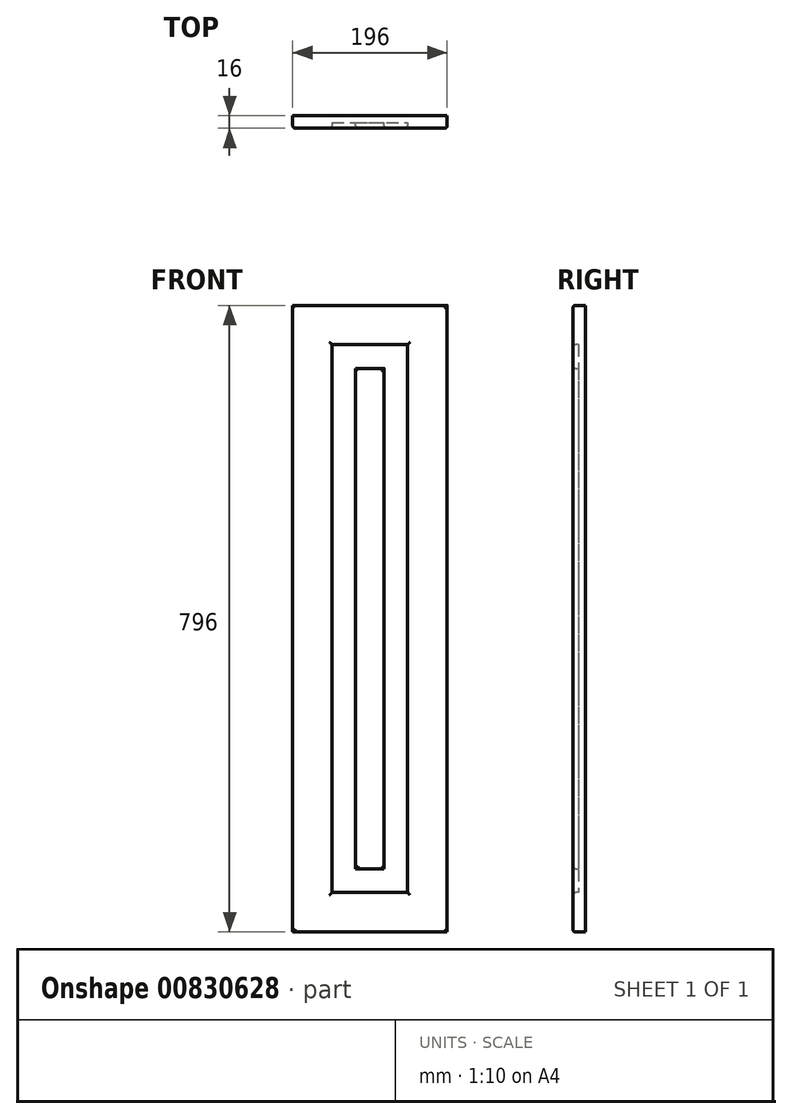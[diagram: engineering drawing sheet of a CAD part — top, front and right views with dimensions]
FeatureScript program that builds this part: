
annotation { "Feature Type Name" : "Feature", "Feature Type Description" : "" }
export const myFeature = defineFeature(function(context is Context, id is Id, definition is map)
    precondition{}
    {
        {
            var Q0;
            Q0=qCreatedBy(makeId("Front.planeOp"),FACE);
            var sketch = newSketch(context, id + "F0", { "sketchPlane" : qUnion([Q0])});
            skLineSegment(sketch, "E0.bottom", {"start": v(0, 0) * mm, "end": v(44.66, 0) * mm});
            skLineSegment(sketch, "E0.top", {"start": v(0, 33.8) * mm, "end": v(44.66, 33.8) * mm});
            skLineSegment(sketch, "E0.left", {"start": v(0, 0) * mm, "end": v(0, 33.8) * mm});
            skLineSegment(sketch, "E0.right", {"start": v(44.66, 0) * mm, "end": v(44.66, 33.8) * mm});
            skSolve(sketch);
        }
        {
            var Q0;
            Q0=makeQuery(id+"F0.imprint","IMPRINT",FACE,{"disambiguationData":[TD([[makeQuery(id+"F0.imprint","IMPRINT",EDGE,{"derivedFrom":sQuery(id+"F0.wireOp",EDGE,"E0.bottom")}),1.0]])]});
            extrude(context, id + "F1", {"entities" : qUnion([Q0]), "depth" : 16 * mm, "offsetDistance" : 25.4 * mm});
        }
        {
            var Q0;
            Q0=makeQuery(id+"F1.opExtrude","SWEPT_FACE",FACE,{"disambiguationData":[OSD([sQuery(id+"F0.wireOp",EDGE,"E0.bottom")])]});
            extrude(context, id + "F2", {"entities" : qUnion([Q0]), "operationType" : NewBodyOperationType.ADD, "oppositeDirection" : true, "depth" : 796 * mm, "offsetDistance" : 25 * mm});
        }
        {
            var Q0;
            {var subQ0=sQuery(id+"F0.wireOp",EDGE,"E0.left");Q0=makeQuery(id+"F2.boolean.opBoolean","MERGE",FACE,{"derivedFrom":[makeQuery(id+"F1.opExtrude","SWEPT_FACE",FACE,{"disambiguationData":[OSD([subQ0])]}),makeQuery(id+"F2.opExtrude","SWEPT_FACE",FACE,{"disambiguationData":[OSD([sQuery(id+"F0.wireOp",EDGE,"E0.bottom"),subQ0])]})]});}
            extrude(context, id + "F3", {"entities" : qUnion([Q0]), "operationType" : NewBodyOperationType.ADD, "oppositeDirection" : true, "depth" : 196 * mm, "offsetDistance" : 25 * mm});
        }
        {
            var Q0;
            {var subQ0=sQuery(id+"F0.wireOp",EDGE,"E0.left");var subQ1=sQuery(id+"F0.wireOp",EDGE,"E0.bottom");Q0=makeQuery(id+"F3.boolean.opBoolean","MERGE",FACE,{"derivedFrom":[makeQuery(id+"F2.boolean.opBoolean","MERGE",FACE,{"derivedFrom":[makeQuery(id+"F1.opExtrude","CAP_FACE",FACE,{"disambiguationData":[OSD([subQ1,sQuery(id+"F0.wireOp",EDGE,"E0.top"),subQ0,sQuery(id+"F0.wireOp",EDGE,"E0.right")])],"isStart":false}),makeQuery(id+"F2.opExtrude","SWEPT_FACE",FACE,{"disambiguationData":[OSD([subQ1]),TDD([makeQuery(id+"F1.opExtrude","CAP_EDGE",EDGE,{"disambiguationData":[OSD([subQ1])],"isStart":false})])]})]}),makeQuery(id+"F3.opExtrude","SWEPT_FACE",FACE,{"disambiguationData":[OSD([subQ1,subQ0]),TDD([makeQuery(id+"F2.boolean.opBoolean","MERGE",EDGE,{"derivedFrom":[makeQuery(id+"F1.opExtrude","CAP_EDGE",EDGE,{"disambiguationData":[OSD([subQ0])],"isStart":false}),makeQuery(id+"F2.opExtrude","SWEPT_EDGE",EDGE,{"disambiguationData":[OSD([subQ1,subQ0]),TDD([makeQuery(id+"F1.opExtrude","CAP_VERTEX",VERTEX,{"disambiguationData":[OSD([subQ1,subQ0])],"isStart":false})])]})]})])]})]});}
            var sketch = newSketch(context, id + "F4", { "sketchPlane" : qUnion([Q0])});
            skLineSegment(sketch, "E1.bottom", {"start": v(59.7, 646.67) * mm, "end": v(128.66, 646.67) * mm});
            skLineSegment(sketch, "E1.top", {"start": v(59.7, 152.97) * mm, "end": v(128.66, 152.97) * mm});
            skLineSegment(sketch, "E1.left", {"start": v(59.7, 646.67) * mm, "end": v(59.7, 152.97) * mm});
            skLineSegment(sketch, "E1.right", {"start": v(128.66, 646.67) * mm, "end": v(128.66, 152.97) * mm});
            skSolve(sketch);
        }
        {
            var Q0;
            Q0=makeQuery(id+"F4.imprint","IMPRINT",FACE,{"disambiguationData":[TD([[makeQuery(id+"F4.imprint","IMPRINT",EDGE,{"derivedFrom":sQuery(id+"F4.wireOp",EDGE,"E1.bottom")}),-1.0]])]});
            extrude(context, id + "F5", {"entities" : qUnion([Q0]), "operationType" : NewBodyOperationType.REMOVE, "oppositeDirection" : true, "depth" : 7 * mm, "offsetDistance" : 25 * mm});
        }
        {
            var Q0;
            Q0=makeQuery(id+"F5.boolean.opBoolean","COPY",FACE,{"derivedFrom":makeQuery(id+"F5.opExtrude","SWEPT_FACE",FACE,{"disambiguationData":[OSD([sQuery(id+"F4.wireOp",EDGE,"E1.left")])]})});
            extrude(context, id + "F6", {"entities" : qUnion([Q0]), "operationType" : NewBodyOperationType.REMOVE, "oppositeDirection" : true, "depth" : 9.7 * mm, "offsetDistance" : 25 * mm});
        }
        {
            var Q0;
            {var subQ0=sQuery(id+"F4.wireOp",EDGE,"E1.bottom");Q0=makeQuery(id+"F6.boolean.opBoolean","MERGE",FACE,{"derivedFrom":[makeQuery(id+"F5.boolean.opBoolean","COPY",FACE,{"derivedFrom":makeQuery(id+"F5.opExtrude","SWEPT_FACE",FACE,{"disambiguationData":[OSD([subQ0])]})}),makeQuery(id+"F6.opExtrude","SWEPT_FACE",FACE,{"disambiguationData":[OSD([subQ0,sQuery(id+"F4.wireOp",EDGE,"E1.left")])]})]});}
            extrude(context, id + "F7", {"entities" : qUnion([Q0]), "operationType" : NewBodyOperationType.ADD, "oppositeDirection" : true, "depth" : 99.33 * mm, "offsetDistance" : 25 * mm});
        }
        {
            var Q0;
            {var subQ0=sQuery(id+"F4.wireOp",EDGE,"E1.bottom");Q0=makeQuery(id+"F6.boolean.opBoolean","MERGE",FACE,{"derivedFrom":[makeQuery(id+"F5.boolean.opBoolean","COPY",FACE,{"derivedFrom":makeQuery(id+"F5.opExtrude","SWEPT_FACE",FACE,{"disambiguationData":[OSD([subQ0])]})}),makeQuery(id+"F6.opExtrude","SWEPT_FACE",FACE,{"disambiguationData":[OSD([subQ0,sQuery(id+"F4.wireOp",EDGE,"E1.left")])]})]});}
            extrude(context, id + "F8", {"entities" : qUnion([Q0]), "operationType" : NewBodyOperationType.REMOVE, "oppositeDirection" : true, "depth" : 99.33 * mm, "offsetDistance" : 25 * mm});
        }
        {
            var Q0;
            {var subQ0=sQuery(id+"F4.wireOp",EDGE,"E1.right");Q0=makeQuery(id+"F8.boolean.opBoolean","MERGE",FACE,{"derivedFrom":[makeQuery(id+"F5.boolean.opBoolean","COPY",FACE,{"derivedFrom":makeQuery(id+"F5.opExtrude","SWEPT_FACE",FACE,{"disambiguationData":[OSD([subQ0])]})}),makeQuery(id+"F8.opExtrude","SWEPT_FACE",FACE,{"disambiguationData":[OSD([sQuery(id+"F4.wireOp",EDGE,"E1.bottom"),subQ0])]})]});}
            extrude(context, id + "F9", {"entities" : qUnion([Q0]), "operationType" : NewBodyOperationType.REMOVE, "oppositeDirection" : true, "depth" : 17.34 * mm, "offsetDistance" : 25 * mm});
        }
        {
            var Q0;
            {var subQ0=sQuery(id+"F4.wireOp",EDGE,"E1.top");Q0=makeQuery(id+"F9.boolean.opBoolean","MERGE",FACE,{"derivedFrom":[makeQuery(id+"F6.boolean.opBoolean","MERGE",FACE,{"derivedFrom":[makeQuery(id+"F5.boolean.opBoolean","COPY",FACE,{"derivedFrom":makeQuery(id+"F5.opExtrude","SWEPT_FACE",FACE,{"disambiguationData":[OSD([subQ0])]})}),makeQuery(id+"F6.opExtrude","SWEPT_FACE",FACE,{"disambiguationData":[OSD([subQ0,sQuery(id+"F4.wireOp",EDGE,"E1.left")])]})]}),makeQuery(id+"F9.opExtrude","SWEPT_FACE",FACE,{"disambiguationData":[OSD([subQ0,sQuery(id+"F4.wireOp",EDGE,"E1.right")])]})]});}
            extrude(context, id + "F10", {"entities" : qUnion([Q0]), "operationType" : NewBodyOperationType.REMOVE, "oppositeDirection" : true, "depth" : 102.97 * mm, "offsetDistance" : 25 * mm});
        }
        {
            var Q0;
            {var subQ0=sQuery(id+"F4.wireOp",EDGE,"E1.right");var subQ1=sQuery(id+"F4.wireOp",EDGE,"E1.top");var subQ2=sQuery(id+"F4.wireOp",EDGE,"E1.left");var subQ3=sQuery(id+"F4.wireOp",EDGE,"E1.bottom");Q0=makeQuery(id+"F10.boolean.opBoolean","MERGE",FACE,{"derivedFrom":[makeQuery(id+"F9.boolean.opBoolean","MERGE",FACE,{"derivedFrom":[makeQuery(id+"F8.boolean.opBoolean","MERGE",FACE,{"derivedFrom":[makeQuery(id+"F6.boolean.opBoolean","MERGE",FACE,{"derivedFrom":[makeQuery(id+"F5.boolean.opBoolean","COPY",FACE,{"derivedFrom":makeQuery(id+"F5.opExtrude","CAP_FACE",FACE,{"disambiguationData":[OSD([subQ3,subQ1,subQ2,subQ0])],"isStart":false})}),makeQuery(id+"F6.opExtrude","SWEPT_FACE",FACE,{"disambiguationData":[OSD([subQ2]),TDD([makeQuery(id+"F5.boolean.opBoolean","COPY",EDGE,{"derivedFrom":makeQuery(id+"F5.opExtrude","CAP_EDGE",EDGE,{"disambiguationData":[OSD([subQ2])],"isStart":false})})])]})]}),makeQuery(id+"F8.opExtrude","SWEPT_FACE",FACE,{"disambiguationData":[OSD([subQ3,subQ2]),TDD([makeQuery(id+"F6.boolean.opBoolean","MERGE",EDGE,{"derivedFrom":[makeQuery(id+"F5.boolean.opBoolean","COPY",EDGE,{"derivedFrom":makeQuery(id+"F5.opExtrude","CAP_EDGE",EDGE,{"disambiguationData":[OSD([subQ3])],"isStart":false})}),makeQuery(id+"F6.opExtrude","SWEPT_EDGE",EDGE,{"disambiguationData":[OSD([subQ3,subQ2]),TDD([makeQuery(id+"F5.boolean.opBoolean","COPY",VERTEX,{"derivedFrom":makeQuery(id+"F5.opExtrude","CAP_VERTEX",VERTEX,{"disambiguationData":[OSD([subQ3,subQ2])],"isStart":false})})])]})]})])]})]}),makeQuery(id+"F9.opExtrude","SWEPT_FACE",FACE,{"disambiguationData":[OSD([subQ3,subQ0]),TDD([makeQuery(id+"F8.boolean.opBoolean","MERGE",EDGE,{"derivedFrom":[makeQuery(id+"F5.boolean.opBoolean","COPY",EDGE,{"derivedFrom":makeQuery(id+"F5.opExtrude","CAP_EDGE",EDGE,{"disambiguationData":[OSD([subQ0])],"isStart":false})}),makeQuery(id+"F8.opExtrude","SWEPT_EDGE",EDGE,{"disambiguationData":[OSD([subQ3,subQ0]),TDD([makeQuery(id+"F5.boolean.opBoolean","COPY",VERTEX,{"derivedFrom":makeQuery(id+"F5.opExtrude","CAP_VERTEX",VERTEX,{"disambiguationData":[OSD([subQ3,subQ0])],"isStart":false})})])]})]})])]})]}),makeQuery(id+"F10.opExtrude","SWEPT_FACE",FACE,{"disambiguationData":[OSD([subQ1,subQ2,subQ0]),TDD([makeQuery(id+"F9.boolean.opBoolean","MERGE",EDGE,{"derivedFrom":[makeQuery(id+"F6.boolean.opBoolean","MERGE",EDGE,{"derivedFrom":[makeQuery(id+"F5.boolean.opBoolean","COPY",EDGE,{"derivedFrom":makeQuery(id+"F5.opExtrude","CAP_EDGE",EDGE,{"disambiguationData":[OSD([subQ1])],"isStart":false})}),makeQuery(id+"F6.opExtrude","SWEPT_EDGE",EDGE,{"disambiguationData":[OSD([subQ1,subQ2]),TDD([makeQuery(id+"F5.boolean.opBoolean","COPY",VERTEX,{"derivedFrom":makeQuery(id+"F5.opExtrude","CAP_VERTEX",VERTEX,{"disambiguationData":[OSD([subQ1,subQ2])],"isStart":false})})])]})]}),makeQuery(id+"F9.opExtrude","SWEPT_EDGE",EDGE,{"disambiguationData":[OSD([subQ1,subQ0]),TDD([makeQuery(id+"F5.boolean.opBoolean","COPY",VERTEX,{"derivedFrom":makeQuery(id+"F5.opExtrude","CAP_VERTEX",VERTEX,{"disambiguationData":[OSD([subQ1,subQ0])],"isStart":false})})])]})]})])]})]});}
            var sketch = newSketch(context, id + "F11", { "sketchPlane" : qUnion([Q0])});
            skLineSegment(sketch, "E2.bottom", {"start": v(74.13, 678.73) * mm, "end": v(109.41, 678.73) * mm});
            skLineSegment(sketch, "E2.top", {"start": v(74.13, 186.63) * mm, "end": v(109.41, 186.63) * mm});
            skLineSegment(sketch, "E2.left", {"start": v(74.13, 678.73) * mm, "end": v(74.13, 186.63) * mm});
            skLineSegment(sketch, "E2.right", {"start": v(109.41, 678.73) * mm, "end": v(109.41, 186.63) * mm});
            skSolve(sketch);
        }
        {
            var Q0;
            Q0=makeQuery(id+"F11.imprint","IMPRINT",FACE,{"disambiguationData":[TD([[makeQuery(id+"F11.imprint","IMPRINT",EDGE,{"derivedFrom":sQuery(id+"F11.wireOp",EDGE,"E2.bottom")}),-1.0]])]});
            extrude(context, id + "F12", {"entities" : qUnion([Q0]), "operationType" : NewBodyOperationType.ADD, "depth" : 7 * mm, "offsetDistance" : 25 * mm});
        }
        {
            var Q0;
            Q0=makeQuery(id+"F12.opExtrude","SWEPT_FACE",FACE,{"disambiguationData":[OSD([sQuery(id+"F11.wireOp",EDGE,"E2.bottom")])]});
            extrude(context, id + "F13", {"entities" : qUnion([Q0]), "operationType" : NewBodyOperationType.ADD, "depth" : 37.27 * mm, "offsetDistance" : 25 * mm});
        }
        {
            var Q0;
            {var subQ0=sQuery(id+"F11.wireOp",EDGE,"E2.right");Q0=makeQuery(id+"F13.boolean.opBoolean","MERGE",FACE,{"derivedFrom":[makeQuery(id+"F12.opExtrude","SWEPT_FACE",FACE,{"disambiguationData":[OSD([subQ0])]}),makeQuery(id+"F13.opExtrude","SWEPT_FACE",FACE,{"disambiguationData":[OSD([sQuery(id+"F11.wireOp",EDGE,"E2.bottom"),subQ0])]})]});}
            extrude(context, id + "F14", {"entities" : qUnion([Q0]), "operationType" : NewBodyOperationType.ADD, "depth" : 6.58 * mm, "offsetDistance" : 25 * mm});
        }
        {
            var Q0;
            {var subQ0=sQuery(id+"F11.wireOp",EDGE,"E2.top");Q0=makeQuery(id+"F14.boolean.opBoolean","MERGE",FACE,{"derivedFrom":[makeQuery(id+"F12.opExtrude","SWEPT_FACE",FACE,{"disambiguationData":[OSD([subQ0])]}),makeQuery(id+"F14.opExtrude","SWEPT_FACE",FACE,{"disambiguationData":[OSD([subQ0,sQuery(id+"F11.wireOp",EDGE,"E2.right")])]})]});}
            extrude(context, id + "F15", {"entities" : qUnion([Q0]), "operationType" : NewBodyOperationType.ADD, "depth" : 106.63 * mm, "offsetDistance" : 25 * mm});
        }
        {
            var Q0;
            {var subQ0=sQuery(id+"F11.wireOp",EDGE,"E2.left");Q0=makeQuery(id+"F15.boolean.opBoolean","MERGE",FACE,{"derivedFrom":[makeQuery(id+"F13.boolean.opBoolean","MERGE",FACE,{"derivedFrom":[makeQuery(id+"F12.opExtrude","SWEPT_FACE",FACE,{"disambiguationData":[OSD([subQ0])]}),makeQuery(id+"F13.opExtrude","SWEPT_FACE",FACE,{"disambiguationData":[OSD([sQuery(id+"F11.wireOp",EDGE,"E2.bottom"),subQ0])]})]}),makeQuery(id+"F15.opExtrude","SWEPT_FACE",FACE,{"disambiguationData":[OSD([sQuery(id+"F11.wireOp",EDGE,"E2.top"),subQ0])]})]});}
            extrude(context, id + "F16", {"entities" : qUnion([Q0]), "operationType" : NewBodyOperationType.REMOVE, "oppositeDirection" : true, "depth" : 5.87 * mm, "offsetDistance" : 25 * mm});
        }
        {
            var Q0;
            {var subQ0=sQuery(id+"F0.wireOp",EDGE,"E0.left");var subQ1=sQuery(id+"F0.wireOp",EDGE,"E0.bottom");Q0=makeQuery(id+"F3.boolean.opBoolean","MERGE",FACE,{"derivedFrom":[makeQuery(id+"F2.boolean.opBoolean","MERGE",FACE,{"derivedFrom":[makeQuery(id+"F1.opExtrude","CAP_FACE",FACE,{"disambiguationData":[OSD([subQ1,sQuery(id+"F0.wireOp",EDGE,"E0.top"),subQ0,sQuery(id+"F0.wireOp",EDGE,"E0.right")])],"isStart":false}),makeQuery(id+"F2.opExtrude","SWEPT_FACE",FACE,{"disambiguationData":[OSD([subQ1]),TDD([makeQuery(id+"F1.opExtrude","CAP_EDGE",EDGE,{"disambiguationData":[OSD([subQ1])],"isStart":false})])]})]}),makeQuery(id+"F3.opExtrude","SWEPT_FACE",FACE,{"disambiguationData":[OSD([subQ1,subQ0]),TDD([makeQuery(id+"F2.boolean.opBoolean","MERGE",EDGE,{"derivedFrom":[makeQuery(id+"F1.opExtrude","CAP_EDGE",EDGE,{"disambiguationData":[OSD([subQ0])],"isStart":false}),makeQuery(id+"F2.opExtrude","SWEPT_EDGE",EDGE,{"disambiguationData":[OSD([subQ1,subQ0]),TDD([makeQuery(id+"F1.opExtrude","CAP_VERTEX",VERTEX,{"disambiguationData":[OSD([subQ1,subQ0])],"isStart":false})])]})]})])]})]});}
            var Q1;
            {var subQ0=sQuery(id+"F11.wireOp",EDGE,"E2.right");var subQ1=sQuery(id+"F11.wireOp",EDGE,"E2.top");var subQ2=sQuery(id+"F11.wireOp",EDGE,"E2.bottom");Q1=makeQuery(id+"F15.boolean.opBoolean","MERGE",FACE,{"derivedFrom":[makeQuery(id+"F14.boolean.opBoolean","MERGE",FACE,{"derivedFrom":[makeQuery(id+"F13.boolean.opBoolean","MERGE",FACE,{"derivedFrom":[makeQuery(id+"F12.opExtrude","CAP_FACE",FACE,{"disambiguationData":[OSD([subQ2,subQ1,sQuery(id+"F11.wireOp",EDGE,"E2.left"),subQ0])],"isStart":false}),makeQuery(id+"F13.opExtrude","SWEPT_FACE",FACE,{"disambiguationData":[OSD([subQ2]),TDD([makeQuery(id+"F12.opExtrude","CAP_EDGE",EDGE,{"disambiguationData":[OSD([subQ2])],"isStart":false})])]})]}),makeQuery(id+"F14.opExtrude","SWEPT_FACE",FACE,{"disambiguationData":[OSD([subQ2,subQ0]),TDD([makeQuery(id+"F13.boolean.opBoolean","MERGE",EDGE,{"derivedFrom":[makeQuery(id+"F12.opExtrude","CAP_EDGE",EDGE,{"disambiguationData":[OSD([subQ0])],"isStart":false}),makeQuery(id+"F13.opExtrude","SWEPT_EDGE",EDGE,{"disambiguationData":[OSD([subQ2,subQ0]),TDD([makeQuery(id+"F12.opExtrude","CAP_VERTEX",VERTEX,{"disambiguationData":[OSD([subQ2,subQ0])],"isStart":false})])]})]})])]})]}),makeQuery(id+"F15.opExtrude","SWEPT_FACE",FACE,{"disambiguationData":[OSD([subQ1,subQ0]),TDD([makeQuery(id+"F14.boolean.opBoolean","MERGE",EDGE,{"derivedFrom":[makeQuery(id+"F12.opExtrude","CAP_EDGE",EDGE,{"disambiguationData":[OSD([subQ1])],"isStart":false}),makeQuery(id+"F14.opExtrude","SWEPT_EDGE",EDGE,{"disambiguationData":[OSD([subQ1,subQ0]),TDD([makeQuery(id+"F12.opExtrude","CAP_VERTEX",VERTEX,{"disambiguationData":[OSD([subQ1,subQ0])],"isStart":false})])]})]})])]})]});}
            fillet(context, id + "F17", {"entities" : qUnion([Q0, Q1]), "radius" : 3 * mm, "tangentPropagation" : true, "allowEdgeOverflow" : false});
        }
    });
